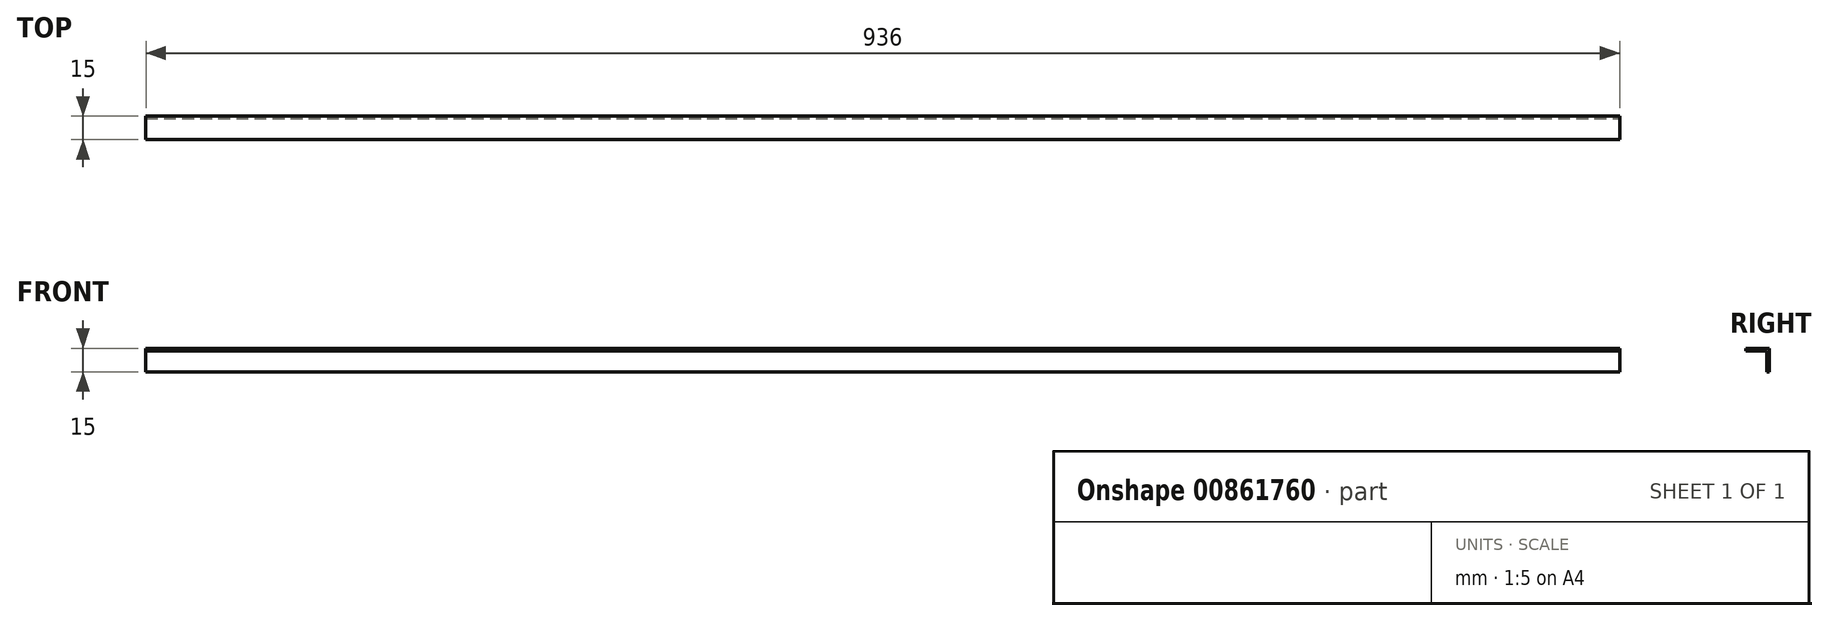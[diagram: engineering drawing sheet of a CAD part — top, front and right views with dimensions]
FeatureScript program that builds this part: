
annotation { "Feature Type Name" : "Feature", "Feature Type Description" : "" }
export const myFeature = defineFeature(function(context is Context, id is Id, definition is map)
    precondition{}
    {
        {
            var Q0;
            Q0=qCreatedBy(makeId("Front.planeOp"),FACE);
            var sketch = newSketch(context, id + "F0", { "sketchPlane" : qUnion([Q0])});
            skLineSegment(sketch, "E0", {"start": v(-21.04, 13.9) * mm, "end": v(-21.04, -1.1) * mm});
            skLineSegment(sketch, "E1", {"start": v(-21.04, -1.1) * mm, "end": v(-6.04, -1.1) * mm});
            skLineSegment(sketch, "E2", {"start": v(-6.04, -1.1) * mm, "end": v(-6.04, 0.5) * mm});
            skLineSegment(sketch, "E3", {"start": v(-6.04, 0.5) * mm, "end": v(-19.44, 0.5) * mm});
            skLineSegment(sketch, "E4", {"start": v(-19.44, 0.5) * mm, "end": v(-19.44, 13.87) * mm});
            skLineSegment(sketch, "E5", {"start": v(-19.44, 13.87) * mm, "end": v(-21.04, 13.9) * mm});
            skSolve(sketch);
        }
        {
            var Q0;
            Q0=makeQuery(id+"F0.imprint","IMPRINT",FACE,{"disambiguationData":[TD([[makeQuery(id+"F0.imprint","IMPRINT",EDGE,{"derivedFrom":sQuery(id+"F0.wireOp",EDGE,"E0")}),1.0]])]});
            extrude(context, id + "F1", {"entities" : qUnion([Q0]), "endBound" : BoundingType.SYMMETRIC, "oppositeDirection" : true, "depth" : 936 * mm, "offsetDistance" : 25 * mm});
        }
        {
            var Q0;
            Q0=makeQuery(id+"F1.opExtrude","SWEPT_BODY",BODY,{"disambiguationData":[OSD([sQuery(id+"F0.wireOp",EDGE,"E0"),sQuery(id+"F0.wireOp",EDGE,"E1"),sQuery(id+"F0.wireOp",EDGE,"E2"),sQuery(id+"F0.wireOp",EDGE,"E3"),sQuery(id+"F0.wireOp",EDGE,"E4"),sQuery(id+"F0.wireOp",EDGE,"E5")])]});
            var Q1;
            Q1=makeQuery(id+"F1.opExtrude","SWEPT_EDGE",EDGE,{"disambiguationData":[OSD([sQuery(id+"F0.wireOp",EDGE,"E0"),sQuery(id+"F0.wireOp",EDGE,"E1")])]});
            transform(context, id + "F2", {"entities" : qUnion([Q0]), "transformType" : TransformType.ROTATION, "transformAxis" : qUnion([Q1]), "angle" : 180 * degree, "makeCopy" : false});
        }
        {
            var Q0;
            Q0=makeQuery(id+"F1.opExtrude","SWEPT_BODY",BODY,{"disambiguationData":[OSD([sQuery(id+"F0.wireOp",EDGE,"E0"),sQuery(id+"F0.wireOp",EDGE,"E1"),sQuery(id+"F0.wireOp",EDGE,"E2"),sQuery(id+"F0.wireOp",EDGE,"E3"),sQuery(id+"F0.wireOp",EDGE,"E4"),sQuery(id+"F0.wireOp",EDGE,"E5")])]});
            var Q1;
            Q1=makeQuery(id+"F1.opExtrude","CAP_EDGE",EDGE,{"disambiguationData":[OSD([sQuery(id+"F0.wireOp",EDGE,"E0")])],"isStart":true});
            transform(context, id + "F3", {"entities" : qUnion([Q0]), "transformType" : TransformType.ROTATION, "transformAxis" : qUnion([Q1]), "angle" : 90 * degree, "makeCopy" : false});
        }
    });
